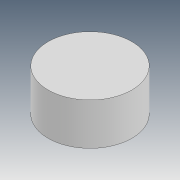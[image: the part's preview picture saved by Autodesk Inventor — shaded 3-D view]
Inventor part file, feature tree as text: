
AUTODESK INVENTOR PART (.ipt)
format: ipt  version: 2021 (Build 250183000, 183)  size: 76,288 bytes
history: native  units: in
note: dims shown in document units (in); Inventor stores cm internally (conversion verified against a paired STEP export)
features: sketch x3, other x1, extrude x1
ambient origin geometry x8: Origin, YZ Plane, XZ Plane, XY Plane, X Axis, Y Axis, Z Axis, Center Point
bodies: Body1 (feature_tree)
feature tree (5):
  other  "Sólido1"
  sketch  "Esboço1"  dims[d0=0.0787in d1=0.0394in d2=0.0in]
  sketch  "Esboço2"
  extrude  "Extrusão1"  Depth=0.0394in TaperAngle=0.0deg
  sketch  "Esboço3"
